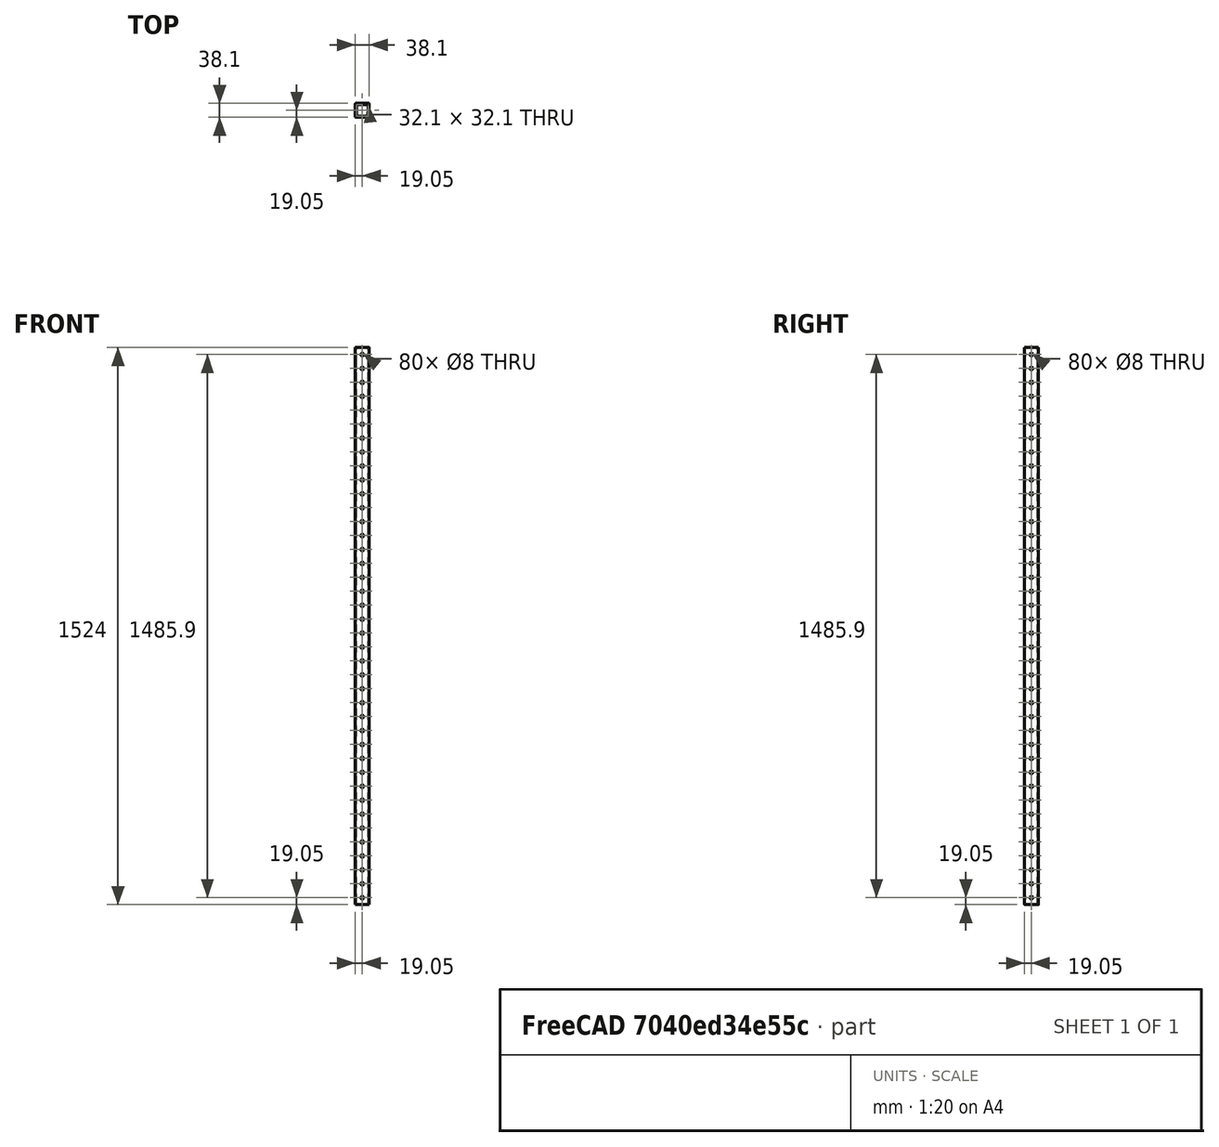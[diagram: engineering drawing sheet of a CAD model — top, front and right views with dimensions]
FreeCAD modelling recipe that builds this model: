
FCSTD DOCUMENT  (FreeCAD 0.15R4671 (Git))
Label: 40x-fillet-hollow
License: All rights reserved
LicenseURL: http://en.wikipedia.org/wiki/All_rights_reserved
objects: Part::Cut×3, Part::Box×2, Part::Cylinder×2, Part::FeaturePython×2, PartDesign::Fillet×1
note: 10 computed .brp shape members not serialized (recipe doc carries the construction recipe); baked Part::Feature solids carry a one-line shape summary decoded from their .brp

FEATURE [Part::Box] Box  label="Beam"
  Height = 1524
  Length = 38.1
  Width = 38.1
FEATURE [Part::Cylinder] Cylinder
  Angle = 360
  Height = 38.1
  Placement = pos=(0,19.05,19.05) rot=(0,1,0;1.5708rad)
  Radius = 4
FEATURE [Part::Cylinder] Cylinder001
  Angle = 360
  Height = 38.1
  Placement = pos=(19.05,38.1,19.05) rot=(1,0,0;1.5708rad)
  Radius = 4
FEATURE [Part::FeaturePython] Array  label="Holes1"  # Draft array (typed FeaturePython)
  Angle = 360
  ArrayType = 0
  Axis = (0,0,1)
  Base = -> Cylinder001
  Center = (0,0,0)
  Fuse = false
  IntervalAxis = (0,0,0)
  IntervalX = (1,0,0)
  IntervalY = (0,1,0)
  IntervalZ = (0,0,38.1)
  NumberPolar = 1
  NumberX = 1
  NumberY = 1
  NumberZ = 40
FEATURE [Part::FeaturePython] Array001  label="Holes2"  # Draft array (typed FeaturePython)
  Angle = 360
  ArrayType = 0
  Axis = (0,0,1)
  Base = -> Cylinder
  Center = (0,0,0)
  Fuse = false
  IntervalAxis = (0,0,0)
  IntervalX = (1,0,0)
  IntervalY = (0,1,0)
  IntervalZ = (0,0,38.1)
  NumberPolar = 1
  NumberX = 1
  NumberY = 1
  NumberZ = 40
FEATURE [Part::Box] Box001  label="Cutout"
  Height = 1524
  Length = 32.1
  Placement = pos=(3,3,0) rot=(0,0,1;0rad)
  Width = 32.1
FEATURE [PartDesign::Fillet] Fillet
  Base = -> Box [Edge1,Edge5,Edge7,Edge3]
  Radius = 1
FEATURE [Part::Cut] Cut
  Base = -> Fillet
  Tool = -> Array
FEATURE [Part::Cut] Cut001
  Base = -> Cut
  Tool = -> Array001
FEATURE [Part::Cut] Cut002
  Base = -> Cut001
  Tool = -> Box001
